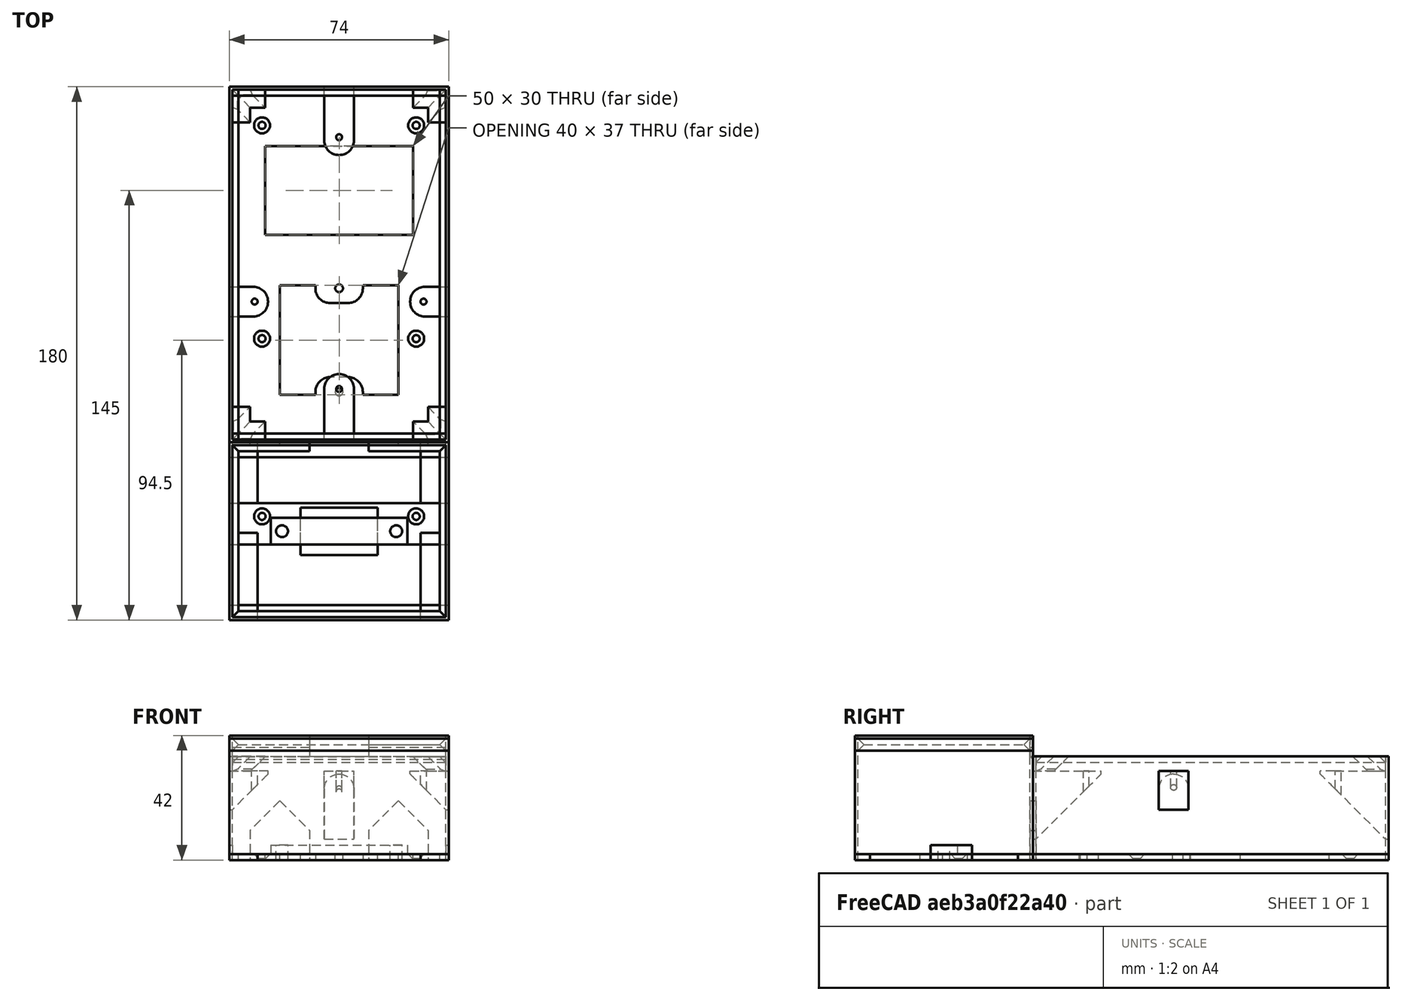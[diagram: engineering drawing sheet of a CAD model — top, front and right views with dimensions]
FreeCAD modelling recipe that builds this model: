
FCSTD DOCUMENT  (FreeCAD 0.16R)
Label: sonoff-T1-US-aufputz-und-Steckdose_v2.4
License: All rights reserved
LicenseURL: http://en.wikipedia.org/wiki/All_rights_reserved
objects: Part::Box×45, Part::Cut×40, Part::Chamfer×28, Part::Cylinder×14, Part::Fillet×5
note: 132 computed .brp shape members not serialized (recipe doc carries the construction recipe); baked Part::Feature solids carry a one-line shape summary decoded from their .brp

FEATURE [Part::Box] Box028  label="Cube023"
  Height = 2
  Length = 72
  Placement = pos=(1,1,33) rot=(0,0,1;0rad)
  Width = 2
FEATURE [Part::Chamfer] Chamfer009
  Base = -> Box028
  Edges = 1 edges r=1.99: [Edge11]
FEATURE [Part::Box] Box037  label="Cube028"
  Height = 2
  Length = 26
  Placement = pos=(24,-38,0) rot=(0,0,1;0rad)
  Width = 16
FEATURE [Part::Cylinder] Cylinder
  Angle = 360
  Height = 10
  Placement = pos=(17.75,-30,0) rot=(0,0,1;0rad)
  Radius = 2
FEATURE [Part::Cylinder] Cylinder001
  Angle = 360
  Height = 10
  Placement = pos=(56.25,-30,0) rot=(0,0,1;0rad)
  Radius = 2
FEATURE [Part::Box] Box038  label="Kragen Stecker"
  Height = 4.1
  Length = 74
  Placement = pos=(0,-60,0) rot=(0,0,1;0rad)
  Width = 60
FEATURE [Part::Box] Box039  label="Kragen Stecker Ausschnitt"
  Height = 4.1
  Length = 68
  Placement = pos=(3,-57,0) rot=(0,0,1;0rad)
  Width = 54
FEATURE [Part::Cut] Cut019
  Base = -> Box038
  Placement = pos=(0,0,36.9) rot=(0,0,1;0rad)
  Tool = -> Box039
FEATURE [Part::Chamfer] Chamfer021
  Base = -> Cut019
  Edges = 4 edges r=2: [Edge10,Edge11,Edge12,Edge13]
FEATURE [Part::Chamfer] Chamfer022  label="Kragen"
  Base = -> Chamfer021
  Edges = 4 edges r=2: [Edge26,Edge29,Edge31,Edge32]
FEATURE [Part::Box] Box045  label="Cube034"
  Height = 4
  Length = 72
  Placement = pos=(1,-1,34) rot=(0,0,1;0rad)
  Width = 1
FEATURE [Part::Chamfer] Chamfer027  label="Verstärkung"
  Base = -> Box045
  Edges = 1 edges r=0.99: [Edge9]
FEATURE [Part::Box] Box032  label="Basis Stecker"
  Height = 42
  Length = 74
  Placement = pos=(0,-60,0) rot=(0,0,1;0rad)
  Width = 60
FEATURE [Part::Box] Box033  label="Ausschnitt Stecker"
  Height = 42
  Length = 72
  Placement = pos=(1,-59,0) rot=(0,0,1;0rad)
  Width = 58
FEATURE [Part::Cut] Cut014
  Base = -> Box032
  Tool = -> Box033
FEATURE [Part::Box] Box  label="Basis"
  Height = 35
  Length = 74
  Width = 120
FEATURE [Part::Box] Box001  label="Ausschnitt"
  Height = 35
  Length = 72
  Placement = pos=(1,1,0) rot=(0,0,1;0rad)
  Width = 118
FEATURE [Part::Cut] Cut
  Base = -> Box
  Tool = -> Box001
FEATURE [Part::Box] Box024  label="Cube019"
  Height = 5
  Length = 5
  Placement = pos=(63,109,30) rot=(0,0,1;0rad)
  Width = 5
FEATURE [Part::Box] Box025  label="Cube020"
  Height = 5
  Length = 11
  Placement = pos=(63,109,30) rot=(0,0,1;0rad)
  Width = 11
FEATURE [Part::Cut] Cut012
  Base = -> Box025
  Tool = -> Box024
FEATURE [Part::Chamfer] Chamfer004
  Base = -> Cut012
  Edges = 4 edges r=4.9: [Edge4,Edge5,Edge15,Edge16]
  Placement = pos=(-1,-1,0) rot=(0,0,1;0rad)
FEATURE [Part::Box] Box046  label="Cube035"
  Height = 2
  Length = 72
  Placement = pos=(1,1,33) rot=(0,0,1;0rad)
  Width = 2
FEATURE [Part::Box] Box029  label="Cube024"
  Height = 2
  Length = 2
  Placement = pos=(1,1,33) rot=(0,0,1;0rad)
  Width = 118
FEATURE [Part::Box] Box030  label="Cube025"
  Height = 2
  Length = 72
  Placement = pos=(1,117,33) rot=(0,0,1;0rad)
  Width = 2
FEATURE [Part::Box] Box031  label="Cube026"
  Height = 2
  Length = 2
  Placement = pos=(71,1,33) rot=(0,0,1;0rad)
  Width = 118
FEATURE [Part::Chamfer] Chamfer008
  Base = -> Box031
  Edges = 1 edges r=1.9: [Edge4]
FEATURE [Part::Chamfer] Chamfer028
  Base = -> Box030
  Edges = 1 edges r=1.9: [Edge9]
FEATURE [Part::Chamfer] Chamfer010
  Base = -> Box029
  Edges = 1 edges r=1.9: [Edge8]
FEATURE [Part::Chamfer] Chamfer011
  Base = -> Box046
  Edges = 1 edges r=1.9: [Edge11]
FEATURE [Part::Box] Box047  label="Cube036"
  Height = 5
  Length = 11
  Placement = pos=(63,109,30) rot=(0,0,1;0rad)
  Width = 11
FEATURE [Part::Box] Box048  label="Cube037"
  Height = 5
  Length = 5
  Placement = pos=(63,109,30) rot=(0,0,1;0rad)
  Width = 5
FEATURE [Part::Cut] Cut013
  Base = -> Box047
  Tool = -> Box048
FEATURE [Part::Chamfer] Chamfer012
  Base = -> Cut013
  Edges = 4 edges r=4.9: [Edge4,Edge5,Edge15,Edge16]
  Placement = pos=(121,45,0) rot=(0,0,1;1.5708rad)
FEATURE [Part::Chamfer] Chamfer013
  Base = -> Chamfer004
  Edges = 2 edges r=0.9: [Edge19,Edge23]
FEATURE [Part::Chamfer] Chamfer014
  Base = -> Chamfer012
  Edges = 2 edges r=0.9: [Edge19,Edge23]
FEATURE [Part::Box] Box034  label="Cube029"
  Height = 5
  Length = 5
  Placement = pos=(63,109,30) rot=(0,0,1;0rad)
  Width = 5
FEATURE [Part::Box] Box035  label="Cube030"
  Height = 5
  Length = 11
  Placement = pos=(63,109,30) rot=(0,0,1;0rad)
  Width = 11
FEATURE [Part::Cut] Cut020
  Base = -> Box035
  Tool = -> Box034
FEATURE [Part::Chamfer] Chamfer015
  Base = -> Cut020
  Edges = 4 edges r=4.9: [Edge4,Edge5,Edge15,Edge16]
  Placement = pos=(-1,-1,0) rot=(0,0,1;0rad)
FEATURE [Part::Chamfer] Chamfer016
  Base = -> Chamfer015
  Edges = 2 edges r=0.9: [Edge19,Edge23]
  Placement = pos=(74,120,0) rot=(0,0,1;3.14159rad)
FEATURE [Part::Box] Box049  label="Cube031"
  Height = 5
  Length = 5
  Placement = pos=(63,109,30) rot=(0,0,1;0rad)
  Width = 5
FEATURE [Part::Box] Box050  label="Cube032"
  Height = 5
  Length = 11
  Placement = pos=(63,109,30) rot=(0,0,1;0rad)
  Width = 11
FEATURE [Part::Cut] Cut015
  Base = -> Box050
  Tool = -> Box049
FEATURE [Part::Chamfer] Chamfer017
  Base = -> Cut015
  Edges = 4 edges r=4.9: [Edge4,Edge5,Edge15,Edge16]
  Placement = pos=(-1,-1,0) rot=(0,0,1;0rad)
FEATURE [Part::Chamfer] Chamfer018
  Base = -> Chamfer017
  Edges = 2 edges r=0.9: [Edge19,Edge23]
  Placement = pos=(-46,74,0) rot=(0,0,-1;1.5708rad)
FEATURE [Part::Box] Box051  label="Cube"
  Height = 13
  Length = 13
  Placement = pos=(0,42.5,17) rot=(0,0,1;0rad)
  Width = 10
FEATURE [Part::Box] Box052  label="Cube033"
  Height = 13
  Length = 13
  Placement = pos=(61,42.5,17) rot=(0,0,1;0rad)
  Width = 10
FEATURE [Part::Box] Box040  label="Cube038"
  Height = 23
  Length = 10
  Placement = pos=(32,0,7) rot=(0,0,1;0rad)
  Width = 23
FEATURE [Part::Box] Box041  label="Cube039"
  Height = 23
  Length = 10
  Placement = pos=(32,97,7) rot=(0,0,1;0rad)
  Width = 23
FEATURE [Part::Chamfer] Chamfer019
  Base = -> Box040
  Edges = 1 edges r=22: [Edge11]
FEATURE [Part::Chamfer] Chamfer020
  Base = -> Box041
  Edges = 1 edges r=22: [Edge9]
FEATURE [Part::Chamfer] Chamfer029
  Base = -> Box051
  Edges = 1 edges r=12: [Edge8]
FEATURE [Part::Chamfer] Chamfer030
  Base = -> Box052
  Edges = 1 edges r=12: [Edge4]
FEATURE [Part::Cylinder] Cylinder002
  Angle = 360
  Height = 40
  Placement = pos=(37,18,0) rot=(0,0,1;0rad)
  Radius = 1
FEATURE [Part::Cylinder] Cylinder003
  Angle = 360
  Height = 40
  Placement = pos=(37,103,0) rot=(0,0,1;0rad)
  Radius = 1
FEATURE [Part::Cylinder] Cylinder004
  Angle = 360
  Height = 40
  Placement = pos=(8.5,47.5,0) rot=(0,0,1;0rad)
  Radius = 1
FEATURE [Part::Cylinder] Cylinder005
  Angle = 360
  Height = 40
  Placement = pos=(65.5,47.5,0) rot=(0,0,1;0rad)
  Radius = 1
FEATURE [Part::Cut] Cut021
  Base = -> Chamfer019
  Tool = -> Cylinder002
FEATURE [Part::Cut] Cut022
  Base = -> Chamfer030
  Tool = -> Cylinder005
FEATURE [Part::Cut] Cut018
  Base = -> Chamfer029
  Tool = -> Cylinder004
FEATURE [Part::Cut] Cut023
  Base = -> Chamfer020
  Tool = -> Cylinder003
FEATURE [Part::Box] Box054  label="Cube041"
  Height = 20
  Length = 20
  Placement = pos=(7,-5,0) rot=(0,0,1;0rad)
  Width = 10
FEATURE [Part::Box] Box055  label="Cube042"
  Height = 20
  Length = 20
  Placement = pos=(47,-5,0) rot=(0,0,1;0rad)
  Width = 10
FEATURE [Part::Chamfer] Chamfer033
  Base = -> Box054
  Edges = 2 edges r=9.99: [Edge2,Edge6]
FEATURE [Part::Chamfer] Chamfer034
  Base = -> Box055
  Edges = 2 edges r=9.99: [Edge2,Edge6]
FEATURE [Part::Cut] Cut029
  Base = -> Cut
  Tool = -> Chamfer033
FEATURE [Part::Cut] Cut030
  Base = -> Cut029
  Tool = -> Chamfer033
FEATURE [Part::Cut] Cut031
  Base = -> Cut030
  Tool = -> Chamfer034
FEATURE [Part::Cut] Cut032
  Base = -> Cut014
  Tool = -> Chamfer033
FEATURE [Part::Cut] Cut033
  Base = -> Cut032
  Tool = -> Chamfer034
FEATURE [Part::Box] Box056  label="Cube043"
  Height = 10
  Length = 20
  Placement = pos=(27,-5,35) rot=(0,0,1;0rad)
  Width = 10
FEATURE [Part::Cut] Cut034
  Base = -> Chamfer022
  Tool = -> Box056
FEATURE [Part::Cut] Cut035
  Base = -> Cut033
  Tool = -> Box056
FEATURE [Part::Cut] Cut036
  Base = -> Chamfer027
  Tool = -> Box056
FEATURE [Part::Box] Box058  label="Cube045"
  Height = 5
  Length = 74
  Placement = pos=(0,-34.5,0) rot=(0,0,1;0rad)
  Width = 14
FEATURE [Part::Box] Box059  label="Cube046"
  Height = 2
  Length = 9.5
  Placement = pos=(0,-60,0) rot=(0,0,1;0rad)
  Width = 60
FEATURE [Part::Box] Box060  label="Cube047"
  Height = 2
  Length = 9.5
  Placement = pos=(64.5,-60,0) rot=(0,0,1;0rad)
  Width = 60
FEATURE [Part::Box] Box061  label="Cube048"
  Height = 2
  Length = 74
  Placement = pos=(0,-5,0) rot=(0,0,1;0rad)
  Width = 5
FEATURE [Part::Box] Box062  label="Cube049"
  Height = 2
  Length = 74
  Placement = pos=(0,-60,0) rot=(0,0,1;0rad)
  Width = 5
FEATURE [Part::Cylinder] Cylinder010
  Angle = 360
  Height = 10
  Placement = pos=(11,-25,0) rot=(0,0,1;0rad)
  Radius = 1.2
FEATURE [Part::Cylinder] Cylinder011
  Angle = 360
  Height = 10
  Placement = pos=(63,-25,0) rot=(0,0,1;0rad)
  Radius = 1.2
FEATURE [Part::Cut] Cut037
  Base = -> Box058
  Tool = -> Cylinder
FEATURE [Part::Cut] Cut038
  Base = -> Cut037
  Tool = -> Cylinder001
FEATURE [Part::Cut] Cut039
  Base = -> Cut038
  Tool = -> Cylinder010
FEATURE [Part::Cut] Cut040
  Base = -> Cut039
  Tool = -> Cylinder011
FEATURE [Part::Cylinder] Cylinder012
  Angle = 360
  Height = 10
  Placement = pos=(11,35,0) rot=(0,0,1;0rad)
  Radius = 1.2
FEATURE [Part::Cylinder] Cylinder013
  Angle = 360
  Height = 10
  Placement = pos=(63,35,0) rot=(0,0,1;0rad)
  Radius = 1.2
FEATURE [Part::Box] Box065  label="Basis002"
  Height = 2
  Length = 74
  Width = 120
FEATURE [Part::Box] Box066  label="Cube052"
  Height = 10
  Length = 40
  Placement = pos=(17,22,0) rot=(0,0,1;0rad)
  Width = 25
FEATURE [Part::Cylinder] Cylinder014
  Angle = 360
  Height = 10
  Placement = pos=(37,17,0) rot=(0,0,1;0rad)
  Radius = 1.3
FEATURE [Part::Cylinder] Cylinder015
  Angle = 360
  Height = 10
  Placement = pos=(37,52,0) rot=(0,0,1;0rad)
  Radius = 1.3
FEATURE [Part::Box] Box067  label="Cube053"
  Height = 10
  Length = 12
  Placement = pos=(17,41,0) rot=(0,0,1;0rad)
  Width = 12
FEATURE [Part::Box] Box068  label="Cube054"
  Height = 10
  Length = 12
  Placement = pos=(45,41,0) rot=(0,0,1;0rad)
  Width = 12
FEATURE [Part::Cut] Cut041
  Base = -> Box065
  Tool = -> Cylinder012
FEATURE [Part::Cut] Cut042
  Base = -> Cut041
  Tool = -> Cylinder013
FEATURE [Part::Cut] Cut043
  Base = -> Cut042
  Tool = -> Box066
FEATURE [Part::Cut] Cut044
  Base = -> Cut043
  Tool = -> Cylinder014
FEATURE [Part::Cut] Cut045
  Base = -> Cut044
  Tool = -> Cylinder015
FEATURE [Part::Cut] Cut046
  Base = -> Cut045
  Tool = -> Box067
FEATURE [Part::Cut] Cut047
  Base = -> Cut046
  Tool = -> Box068
FEATURE [Part::Box] Box069  label="Cube055"
  Height = 10
  Length = 12
  Placement = pos=(17,16,0) rot=(0,0,1;0rad)
  Width = 12
FEATURE [Part::Box] Box070  label="Cube056"
  Height = 10
  Length = 12
  Placement = pos=(45,16,0) rot=(0,0,1;0rad)
  Width = 12
FEATURE [Part::Cut] Cut048
  Base = -> Cut047
  Tool = -> Box069
FEATURE [Part::Cut] Cut049
  Base = -> Cut048
  Tool = -> Box070
FEATURE [Part::Box] Box071  label="Ausschnitt oben"
  Height = 10
  Length = 50
  Placement = pos=(12,70,0) rot=(0,0,1;0rad)
  Width = 30
FEATURE [Part::Cut] Cut050
  Base = -> Cut049
  Tool = -> Box071
FEATURE [Part::Chamfer] Chamfer
  Base = -> Cut050
  Edges = 1 edges r=1.5: [Edge10]
FEATURE [Part::Chamfer] Chamfer035
  Base = -> Chamfer
  Edges = 1 edges r=1.5: [Edge28]
FEATURE [Part::Box] Box072  label="Cube058"
  Height = 10
  Length = 72
  Placement = pos=(1,-25.5,2) rot=(0,0,1;0rad)
  Width = 5
FEATURE [Part::Cut] Cut051
  Base = -> Cut040
  Tool = -> Box072
FEATURE [Part::Box] Box073  label="Cube059"
  Height = 10
  Length = 13
  Placement = pos=(1,-35,2) rot=(0,0,1;0rad)
  Width = 15
FEATURE [Part::Box] Box074  label="Cube060"
  Height = 10
  Length = 13
  Placement = pos=(60,-35,2) rot=(0,0,1;0rad)
  Width = 15
FEATURE [Part::Cut] Cut052
  Base = -> Cut051
  Tool = -> Box073
FEATURE [Part::Chamfer] Chamfer036
  Base = -> Cut052
  Edges = 3 edges r=1.5: [Edge38,Edge50,Edge51]
FEATURE [Part::Cut] Cut053
  Base = -> Chamfer036
  Tool = -> Box074
FEATURE [Part::Chamfer] Chamfer037
  Base = -> Cut053
  Edges = 3 edges r=1.5: [Edge54,Edge68,Edge69]
FEATURE [Part::Fillet] Fillet
  Base = -> Chamfer035
  Edges = 4 edges r=5: [Edge54,Edge58,Edge68,Edge72]
FEATURE [Part::Fillet] Fillet001
  Base = -> Cut021
  Edges = 2 edges r=4.9: [Edge1,Edge6]
FEATURE [Part::Fillet] Fillet002
  Base = -> Cut018
  Edges = 2 edges r=4.9: [Edge1,Edge4]
FEATURE [Part::Fillet] Fillet003
  Base = -> Cut022
  Edges = 2 edges r=4.9: [Edge1,Edge4]
FEATURE [Part::Fillet] Fillet004
  Base = -> Cut023
  Edges = 2 edges r=4.9: [Edge1,Edge6]
FEATURE [Part::Box] Box075  label="Cube061"
  Height = 10
  Length = 10
  Placement = pos=(3,-30.5,0) rot=(0,0,1;0rad)
  Width = 10
FEATURE [Part::Box] Box076  label="Cube062"
  Height = 10
  Length = 10
  Placement = pos=(61,-30.5,0) rot=(0,0,1;0rad)
  Width = 10
FEATURE [Part::Cut] Cut054
  Base = -> Box059
  Tool = -> Box075
FEATURE [Part::Cut] Cut055
  Base = -> Box060
  Tool = -> Box076
FEATURE [Part::Cylinder] Cylinder016
  Angle = 360
  Height = 10
  Placement = pos=(11,107,0) rot=(0,0,1;0rad)
  Radius = 1.2
FEATURE [Part::Cylinder] Cylinder017
  Angle = 360
  Height = 10
  Placement = pos=(63,107,0) rot=(0,0,1;0rad)
  Radius = 1.2
FEATURE [Part::Cut] Cut056
  Base = -> Fillet
  Tool = -> Cylinder016
FEATURE [Part::Cut] Cut057
  Base = -> Cut056
  Tool = -> Cylinder017
FEATURE [Part::Chamfer] Chamfer038
  Base = -> Cut057
  Edges = 1 edges r=1.5: [Edge6]
FEATURE [Part::Chamfer] Chamfer039
  Base = -> Chamfer038
  Edges = 1 edges r=1.5: [Edge6]
